# Revit family: 712-0250-04-201-DN250
name_source: partatom
category: Pipe Accessories
units: mm (PartAtom-declared; Revit-internal decimal feet)

## family parameters
Always vertical = Yes
Cut with Voids When Loaded = No
Part Type = Valve - Breaks Into
Round Connector Dimension = Use Diameter
Shared = No
Work Plane-Based = No

## types (1)
- DN250_PN10/16
    Body_wallthickness = 265 mm  [stored 0.869423 ft]
    DN250_PN10 = 712-0250-04-200
    DN250_PN10/16 = Yes
    DN250_PN16 = 712-0250-04-201
    Description_ = AVK FLANGED PIPE W/LOOSE FLANGES
    FOD = 200 mm  [stored 0.656168 ft]
    Flange_thickness = 26 mm
    ID(Radius) = 125 mm  [stored 0.410105 ft]
    L = 350 mm  [stored 1.14829 ft]
    L_Ref = 120 mm  [stored 0.393701 ft]
    Nominal Diameter(DN) = 250 mm  [stored 0.82021 ft]
    RF_Thick = 4 mm  [stored 0.0131234 ft]
    Rf_Dia = 160 mm  [stored 0.524934 ft]
    Search_Table = 712-0420-001-DN40-300
    URL product pages = https://www.avkvalves.com

note: [stored X ft] marks values corroborated as IEEE doubles in the binary element streams (Revit-internal decimal feet)

## geometry (parser evidence)
native form markers: Sweep x6
no freeform markers — native parametric forms only
